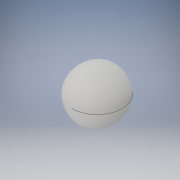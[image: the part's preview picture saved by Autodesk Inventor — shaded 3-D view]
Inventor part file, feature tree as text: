
AUTODESK INVENTOR PART (.ipt)
format: ipt  version: 2017 (Build 210142000, 142)  size: 159,232 bytes
history: native  units: in
note: dims shown in document units (in); Inventor stores cm internally (conversion verified against a paired STEP export)
features: sketch x1, other x1
ambient origin geometry x8: Origin, YZ Plane, XZ Plane, XY Plane, X Axis, Y Axis, Z Axis, Center Point
bodies: Solid1 (feature_tree)
feature tree (2):
  sketch  "Sketch1"  dims[d0=3.75in]
  other  "Form1"
